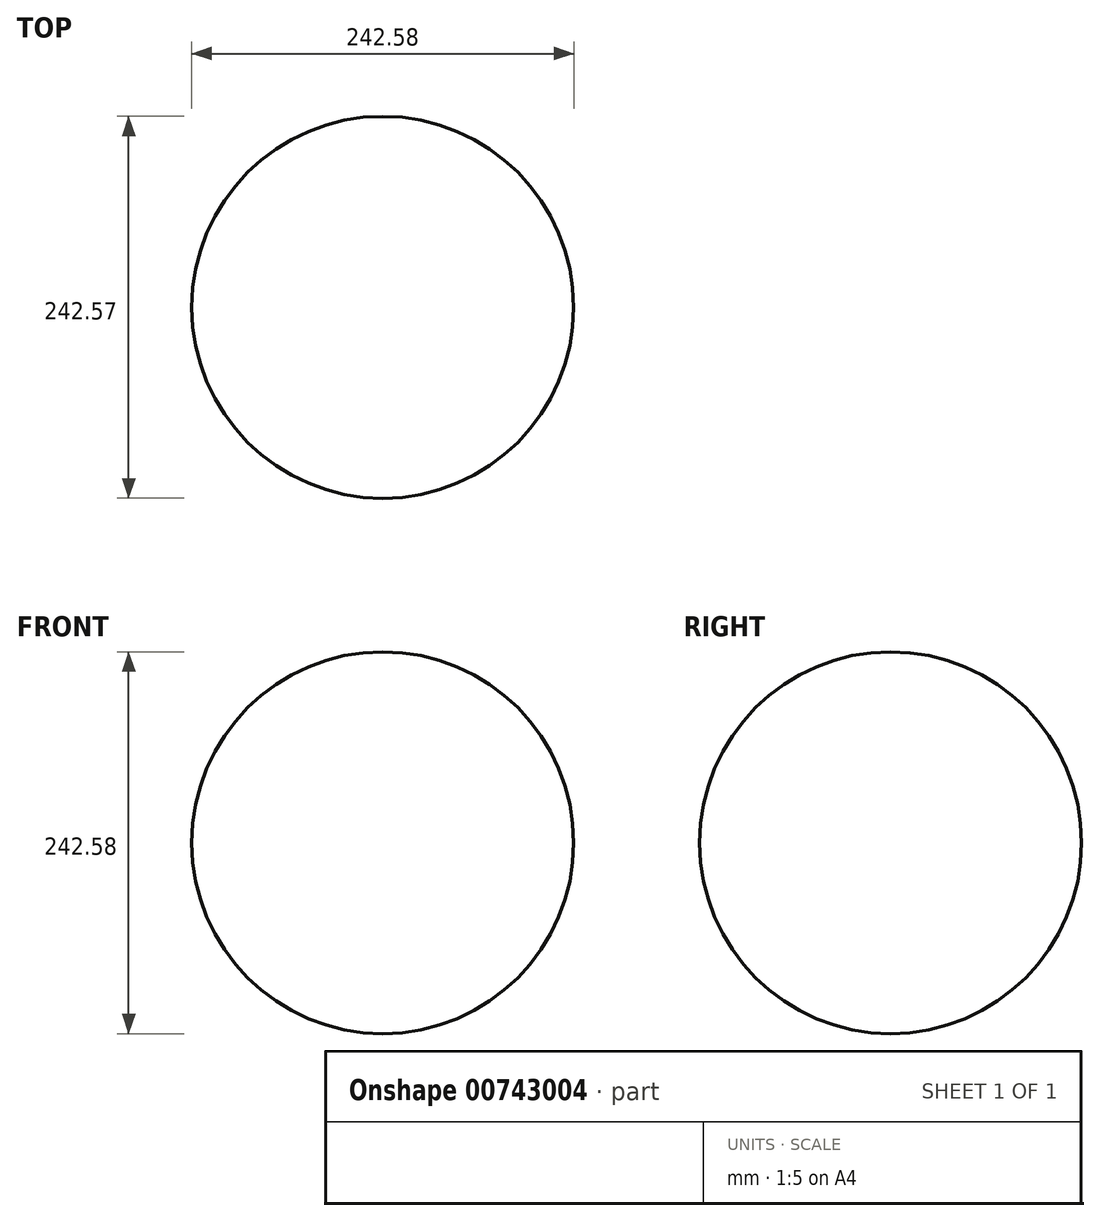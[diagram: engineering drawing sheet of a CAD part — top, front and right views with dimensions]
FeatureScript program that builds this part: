
annotation { "Feature Type Name" : "Feature", "Feature Type Description" : "" }
export const myFeature = defineFeature(function(context is Context, id is Id, definition is map)
    precondition{}
    {
        {
            var Q0;
            Q0=qCreatedBy(makeId("Top.planeOp"),FACE);
            var sketch = newSketch(context, id + "F0", { "sketchPlane" : qUnion([Q0])});
            skCircle(sketch, "E0", {"center": v(0, 0) * mm, "radius": 121.29 * mm});
            skSolve(sketch);
        }
        {
            var Q0;
            Q0=makeQuery(id+"F0.imprint","IMPRINT",FACE,{"disambiguationData":[TD([[makeQuery(id+"F0.imprint","IMPRINT",EDGE,{"derivedFrom":sQuery(id+"F0.wireOp",EDGE,"E0")}),1.0]])]});
            extrude(context, id + "F1", {"entities" : qUnion([Q0]), "depth" : 121.28 * mm, "offsetDistance" : 25.4 * mm, "hasSecondDirection" : true, "secondDirectionOppositeDirection" : true, "secondDirectionDepth" : 121.28 * mm});
        }
        {
            var Q0;
            Q0=makeQuery(id+"F1.opExtrude","CAP_EDGE",EDGE,{"disambiguationData":[OSD([sQuery(id+"F0.wireOp",EDGE,"E0")])],"isStart":false});
            var Q1;
            Q1=makeQuery(id+"F1.opExtrude","CAP_EDGE",EDGE,{"disambiguationData":[OSD([sQuery(id+"F0.wireOp",EDGE,"E0")])],"isStart":true});
            fillet(context, id + "F2", {"entities" : qUnion([Q0, Q1]), "radius" : 121.28 * mm, "tangentPropagation" : true, "allowEdgeOverflow" : false});
        }
    });
